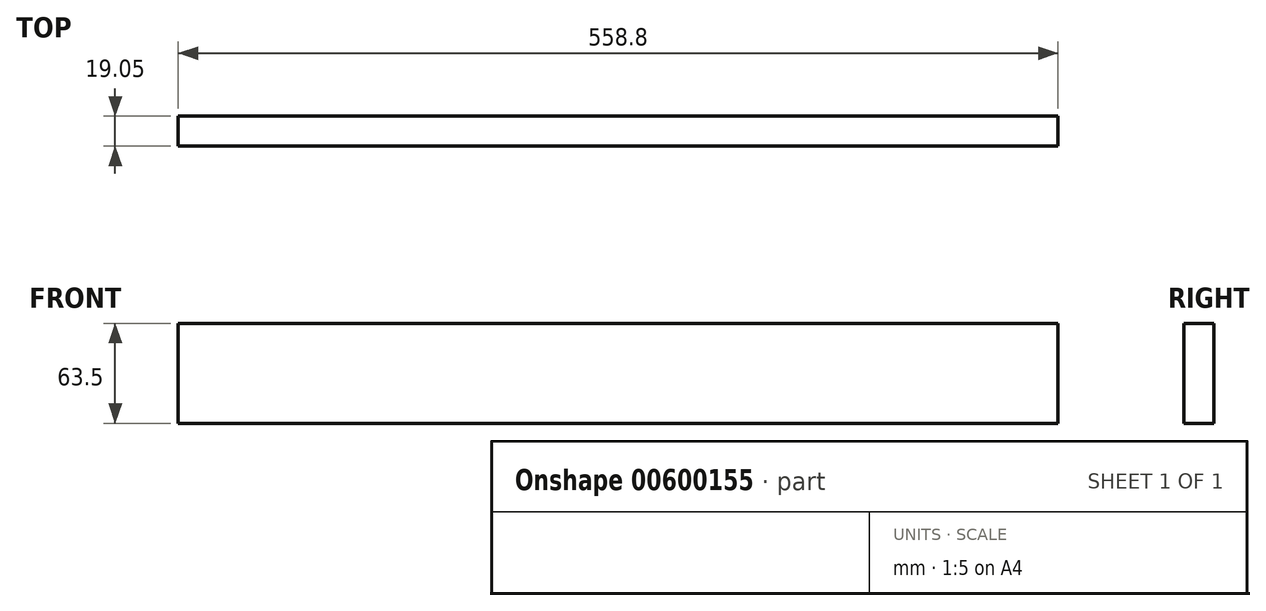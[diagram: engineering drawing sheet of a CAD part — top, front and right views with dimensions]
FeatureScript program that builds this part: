
annotation { "Feature Type Name" : "Feature", "Feature Type Description" : "" }
export const myFeature = defineFeature(function(context is Context, id is Id, definition is map)
    precondition{}
    {
        {
            var Q0;
            Q0=qCreatedBy(makeId("Front.planeOp"),FACE);
            var sketch = newSketch(context, id + "F0", { "sketchPlane" : qUnion([Q0])});
            skLineSegment(sketch, "E0.bottom", {"start": v(-381.64, 53.32) * mm, "end": v(177.16, 53.32) * mm});
            skLineSegment(sketch, "E0.top", {"start": v(-381.64, -10.18) * mm, "end": v(177.16, -10.18) * mm});
            skLineSegment(sketch, "E0.left", {"start": v(-381.64, 53.32) * mm, "end": v(-381.64, -10.18) * mm});
            skLineSegment(sketch, "E0.right", {"start": v(177.16, 53.32) * mm, "end": v(177.16, -10.18) * mm});
            skSolve(sketch);
        }
        {
            var Q0;
            Q0 = qSketchRegion(id + "F0", true);
            extrude(context, id + "F1", {"entities" : qUnion([Q0]), "depth" : 19.05 * mm, "offsetDistance" : 25.4 * mm});
        }
    });
